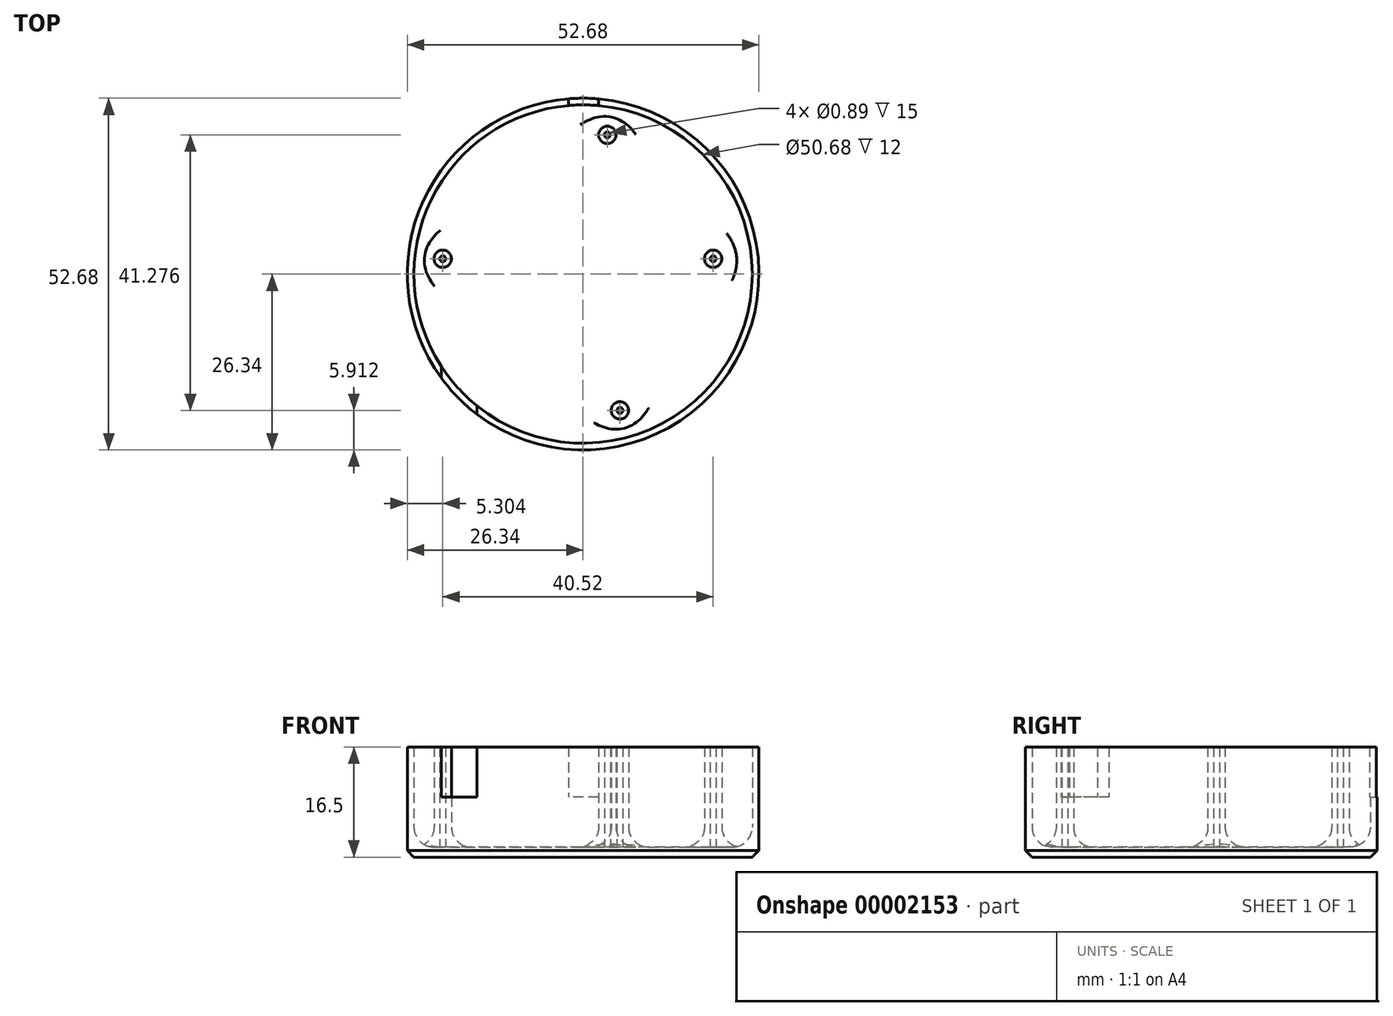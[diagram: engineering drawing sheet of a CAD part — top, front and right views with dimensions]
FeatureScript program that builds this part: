
annotation { "Feature Type Name" : "Feature", "Feature Type Description" : "" }
export const myFeature = defineFeature(function(context is Context, id is Id, definition is map)
    precondition{}
    {
        {
            var Q0;
            Q0=qCreatedBy(makeId("Top.planeOp"),FACE);
            var sketch = newSketch(context, id + "F0", { "sketchPlane" : qUnion([Q0])});
            skCircle(sketch, "E0", {"center": v(3.62, 20.85) * mm, "radius": 0.44 * mm});
            skCircle(sketch, "E1", {"center": v(19.48, 2.3) * mm, "radius": 0.44 * mm});
            skCircle(sketch, "E2", {"center": v(5.52, -20.43) * mm, "radius": 0.45 * mm});
            skCircle(sketch, "E3", {"center": v(-21.04, 2.3) * mm, "radius": 0.45 * mm});
            skCircle(sketch, "E4", {"center": v(5.52, -20.43) * mm, "radius": 1.3 * mm});
            skCircle(sketch, "E5", {"center": v(19.48, 2.3) * mm, "radius": 1.3 * mm});
            skCircle(sketch, "E6", {"center": v(3.62, 20.85) * mm, "radius": 1.3 * mm});
            skCircle(sketch, "E7", {"center": v(-21.04, 2.3) * mm, "radius": 1.3 * mm});
            skCircle(sketch, "E8", {"center": v(0, 0) * mm, "radius": 25.34 * mm, "construction": true});
            skLineSegment(sketch, "E9", {"start": v(-21.04, 2.3) * mm, "end": v(3.62, 20.85) * mm, "construction": true});
            skLineSegment(sketch, "E10", {"start": v(3.62, 20.85) * mm, "end": v(19.48, 2.3) * mm, "construction": true});
            skLineSegment(sketch, "E11", {"start": v(19.48, 2.3) * mm, "end": v(5.52, -20.43) * mm, "construction": true});
            skLineSegment(sketch, "E12", {"start": v(5.52, -20.43) * mm, "end": v(-21.04, 2.3) * mm, "construction": true});
            skLineSegment(sketch, "E13", {"start": v(0, 0) * mm, "end": v(0, 27.69) * mm, "construction": true});
            skLineSegment(sketch, "E14", {"start": v(-21.04, 2.3) * mm, "end": v(19.48, 2.3) * mm, "construction": true});
            skLineSegment(sketch, "E15", {"start": v(5.52, -20.43) * mm, "end": v(3.62, 20.85) * mm, "construction": true});
            skCircle(sketch, "E16", {"center": v(0, 0) * mm, "radius": 21.16 * mm, "construction": true});
            skSolve(sketch);
        }
        {
            var Q0;
            Q0 = qSketchRegion(id + "F0", true);
            extrude(context, id + "F1", {"entities" : qUnion([Q0]), "depth" : 15 * mm});
        }
        {
            var Q0;
            Q0=qCreatedBy(makeId("Top.planeOp"),FACE);
            var sketch = newSketch(context, id + "F2", { "sketchPlane" : qUnion([Q0])});
            skCircle(sketch, "E17", {"center": v(0, 0) * mm, "radius": 25.34 * mm});
            skCircle(sketch, "E18", {"center": v(0, 0) * mm, "radius": 26.34 * mm});
            skSolve(sketch);
        }
        {
            var Q0;
            Q0 = qSketchRegion(id + "F2", true);
            var Q1;
            Q1=makeQuery(id+"F1.opExtrude","CAP_FACE",FACE,{"disambiguationData":[OSD([sQuery(id+"F0.wireOp",EDGE,"E0"),sQuery(id+"F0.wireOp",EDGE,"E6")])],"isStart":false});
            extrude(context, id + "F3", {"entities" : qUnion([Q0]), "endBound" : BoundingType.UP_TO_SURFACE, "endBoundEntityFace" : qUnion([Q1]), "depth" : 15 * mm});
        }
        {
            var Q0;
            Q0=qCreatedBy(makeId("Top.planeOp"),FACE);
            var sketch = newSketch(context, id + "F4", { "sketchPlane" : qUnion([Q0])});
            skCircle(sketch, "E19", {"center": v(0, 0) * mm, "radius": 26.34 * mm});
            skSolve(sketch);
        }
        {
            var Q0;
            Q0 = qSketchRegion(id + "F4", true);
            extrude(context, id + "F5", {"entities" : qUnion([Q0]), "operationType" : NewBodyOperationType.ADD, "oppositeDirection" : true, "depth" : 1.5 * mm});
        }
        {
            var Q0;
            Q0=makeQuery(id+"F5.boolean.opBoolean","SPLIT",FACE,{"disambiguationData":[TD([makeQuery(id+"F1.opExtrude","SWEPT_FACE",FACE,{"disambiguationData":[OSD([sQuery(id+"F0.wireOp",EDGE,"E4")])]})])],"derivedFrom":makeQuery(id+"F5.opExtrude","CAP_FACE",FACE,{"disambiguationData":[OSD([sQuery(id+"F4.wireOp",EDGE,"E19")])],"isStart":true})});
            fillet(context, id + "F6", {"entities" : qUnion([Q0]), "radius" : 3 * mm, "tangentPropagation" : true, "allowEdgeOverflow" : false});
        }
        {
            var Q0;
            Q0=makeQuery(id+"F5.opExtrude","CAP_EDGE",EDGE,{"disambiguationData":[OSD([sQuery(id+"F4.wireOp",EDGE,"E19")])],"isStart":false});
            chamfer(context, id + "F7", {"entities" : qUnion([Q0]), "width" : 1 * mm, "tangentPropagation" : true});
        }
        {
            var Q0;
            Q0=makeQuery(id+"F1.opExtrude","CAP_FACE",FACE,{"disambiguationData":[OSD([sQuery(id+"F0.wireOp",EDGE,"E0"),sQuery(id+"F0.wireOp",EDGE,"E6")])],"isStart":false});
            var sketch = newSketch(context, id + "F8", { "sketchPlane" : qUnion([Q0])});
            skLineSegment(sketch, "E20", {"start": v(3.62, 20.85) * mm, "end": v(2.3, 25.53) * mm, "construction": true});
            skLineSegment(sketch, "E21", {"start": v(2.3, 25.53) * mm, "end": v(-2.18, 25.22) * mm, "construction": true});
            skLineSegment(sketch, "E22", {"start": v(-2.18, 25.22) * mm, "end": v(-21.04, 2.3) * mm, "construction": true});
            skLineSegment(sketch, "E23", {"start": v(-2.18, 25.22) * mm, "end": v(3.62, 20.85) * mm, "construction": true});
            skLineSegment(sketch, "E24.rect.bottom", {"start": v(2.3, 22.79) * mm, "end": v(-2.18, 22.79) * mm});
            skLineSegment(sketch, "E24.rect.top", {"start": v(2.3, 27.97) * mm, "end": v(-2.18, 27.97) * mm});
            skLineSegment(sketch, "E24.rect.left", {"start": v(2.3, 22.79) * mm, "end": v(2.3, 27.97) * mm});
            skLineSegment(sketch, "E24.rect.right", {"start": v(-2.18, 22.79) * mm, "end": v(-2.18, 27.97) * mm});
            skPoint(sketch, "E24.rect.middle", {"position": v(0.07, 25.38) * mm});
            skLineSegment(sketch, "E25", {"start": v(-21.04, 2.3) * mm, "end": v(-21.25, -15.04) * mm, "construction": true});
            skLineSegment(sketch, "E26", {"start": v(-21.25, -15.04) * mm, "end": v(-15.9, -20.4) * mm, "construction": true});
            skLineSegment(sketch, "E27", {"start": v(-15.9, -20.4) * mm, "end": v(5.52, -20.43) * mm, "construction": true});
            skLineSegment(sketch, "E28", {"start": v(-15.9, -20.4) * mm, "end": v(-21.04, 2.3) * mm, "construction": true});
            skLineSegment(sketch, "E29", {"start": v(-21.25, -15.04) * mm, "end": v(-21.25, -31.16) * mm});
            skLineSegment(sketch, "E30", {"start": v(-21.25, -31.16) * mm, "end": v(-15.9, -31.16) * mm});
            skLineSegment(sketch, "E31", {"start": v(-15.9, -31.16) * mm, "end": v(-15.9, -7.46) * mm});
            skLineSegment(sketch, "E32", {"start": v(-15.9, -7.46) * mm, "end": v(-21.25, -7.46) * mm});
            skLineSegment(sketch, "E33", {"start": v(-21.25, -7.46) * mm, "end": v(-21.25, -15.04) * mm});
            skSolve(sketch);
        }
        {
            var Q0;
            Q0 = qSketchRegion(id + "F8", true);
            extrude(context, id + "F9", {"entities" : qUnion([Q0]), "operationType" : NewBodyOperationType.REMOVE, "oppositeDirection" : true, "depth" : 7.5 * mm});
        }
    });
